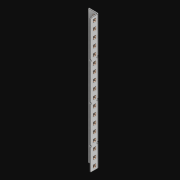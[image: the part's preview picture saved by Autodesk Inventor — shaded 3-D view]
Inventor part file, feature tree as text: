
AUTODESK INVENTOR PART (.ipt)
format: ipt  version: 2021 (Build 250183000, 183)  size: 1,195,008 bytes
history: native  units: in
note: dims shown in document units (in); Inventor stores cm internally (conversion verified against a paired STEP export)
features: extrude x38, other x36, sketch x4, pattern_linear x2, sheet_metal_op x1
ambient origin geometry x8: Origin, YZ Plane, XZ Plane, XY Plane, X Axis, Y Axis, Z Axis, Center Point
bodies: Solid1 (feature_tree)
feature tree (81):
  pattern_linear  "Rectangular Pattern1"  Spacing1=0.5in  [1 undecoded]
  pattern_linear  "Rectangular Pattern3"  Count1=18  [1 undecoded]
  extrude  "Extrusion1"  Depth=0.5in
  extrude  "Extrusion2"  Depth=0.5in
  sketch  "Sketch1"  dims[d0=0.182in]
  other  "Srf1"
  sketch  "Sketch3"  dims[d1=0.063in d2=0.0in]
  other  "Srf3"
  other  "Srf4"
  other  "Srf5"
  other  "Srf6"
  other  "Srf7"
  other  "Srf8"
  other  "Srf9"
  other  "Srf10"
  other  "Srf11"
  other  "Srf12"
  other  "Srf13"
  other  "Srf14"
  other  "Srf15"
  other  "Srf16"
  other  "Srf17"
  other  "Srf18"
  other  "Srf19"
  other  "Srf20"
  other  "Srf142"
  other  "Srf143"
  other  "Srf144"
  other  "Srf145"
  other  "Srf146"
  other  "Srf147"
  other  "Srf148"
  other  "Srf149"
  other  "Srf150"
  other  "Srf151"
  other  "Srf152"
  other  "Srf153"
  other  "Srf154"
  other  "Srf155"
  other  "Srf156"
  other  "Srf157"
  other  "Srf158"
  sketch  "Sketch4"  dims[d6=0.182in]
  sketch  "Sketch5"  dims[d7=0.063in d8=0.0in d11=0.5in d12=0.3937in d14=0.5in d18=7.0866in d20=0.5in d21=8.5in d22=0.0in d23=0.841in d24=0.0in]
  sheet_metal_op  "Fold1"
  extrude  "ExtrusionSrf1"  TaperAngle=0.0deg  [1 undecoded]
  extrude  "ExtrusionSrf3"  Depth=0.5in TaperAngle=0.0deg
  extrude  "ExtrusionSrf4"  [1 undecoded]
  extrude  "ExtrusionSrf5"  [1 undecoded]
  extrude  "ExtrusionSrf6"  [1 undecoded]
  extrude  "ExtrusionSrf7"  [1 undecoded]
  extrude  "ExtrusionSrf8"  [1 undecoded]
  extrude  "ExtrusionSrf9"  [1 undecoded]
  extrude  "ExtrusionSrf10"  [1 undecoded]
  extrude  "ExtrusionSrf11"  [1 undecoded]
  extrude  "ExtrusionSrf12"  [1 undecoded]
  extrude  "ExtrusionSrf13"  [1 undecoded]
  extrude  "ExtrusionSrf14"  [1 undecoded]
  extrude  "ExtrusionSrf15"  [1 undecoded]
  extrude  "ExtrusionSrf16"  [1 undecoded]
  extrude  "ExtrusionSrf17"  [1 undecoded]
  extrude  "ExtrusionSrf18"  [1 undecoded]
  extrude  "ExtrusionSrf19"  [1 undecoded]
  extrude  "ExtrusionSrf20"  [1 undecoded]
  extrude  "ExtrusionSrf142"  [1 undecoded]
  extrude  "ExtrusionSrf143"  [1 undecoded]
  extrude  "ExtrusionSrf144"  [1 undecoded]
  extrude  "ExtrusionSrf145"  [1 undecoded]
  extrude  "ExtrusionSrf146"  [1 undecoded]
  extrude  "ExtrusionSrf147"  [1 undecoded]
  extrude  "ExtrusionSrf148"  [1 undecoded]
  extrude  "ExtrusionSrf149"  [1 undecoded]
  extrude  "ExtrusionSrf150"  [1 undecoded]
  extrude  "ExtrusionSrf151"  [1 undecoded]
  extrude  "ExtrusionSrf152"  [1 undecoded]
  extrude  "ExtrusionSrf153"  [1 undecoded]
  extrude  "ExtrusionSrf154"  [1 undecoded]
  extrude  "ExtrusionSrf155"  [1 undecoded]
  extrude  "ExtrusionSrf156"  [1 undecoded]
  extrude  "ExtrusionSrf157"  [1 undecoded]
  extrude  "ExtrusionSrf158"  [1 undecoded]
note: 37 required parameter values undecoded (feature->parameter linkage not recoverable at this tier; creation-order binding heuristic only, values carry confidence <= 0.55)
